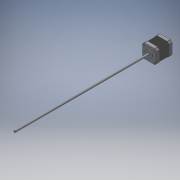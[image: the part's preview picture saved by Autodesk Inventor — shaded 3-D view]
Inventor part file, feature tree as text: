
AUTODESK INVENTOR PART (.ipt)
format: ipt  version: 2019 (Build 230136000, 136)  size: 891,392 bytes
history: native  units: in
note: dims shown in document units (in); Inventor stores cm internally (conversion verified against a paired STEP export)
features: extrude x1, sketch x1
ambient origin geometry x8: Origin, YZ Plane, XZ Plane, XY Plane, X Axis, Y Axis, Z Axis, Center Point
bodies: Solid1 (feature_tree), Solid4 (feature_tree), Solid2 (feature_tree), Solid3 (feature_tree)
feature tree (2):
  extrude  "Extrusion1"  [1 undecoded]
  sketch  "Sketch1"  dims[d0=3.1496in d1=0.0in]
note: 1 required parameter value undecoded (feature->parameter linkage not recoverable at this tier; creation-order binding heuristic only, values carry confidence <= 0.55)
